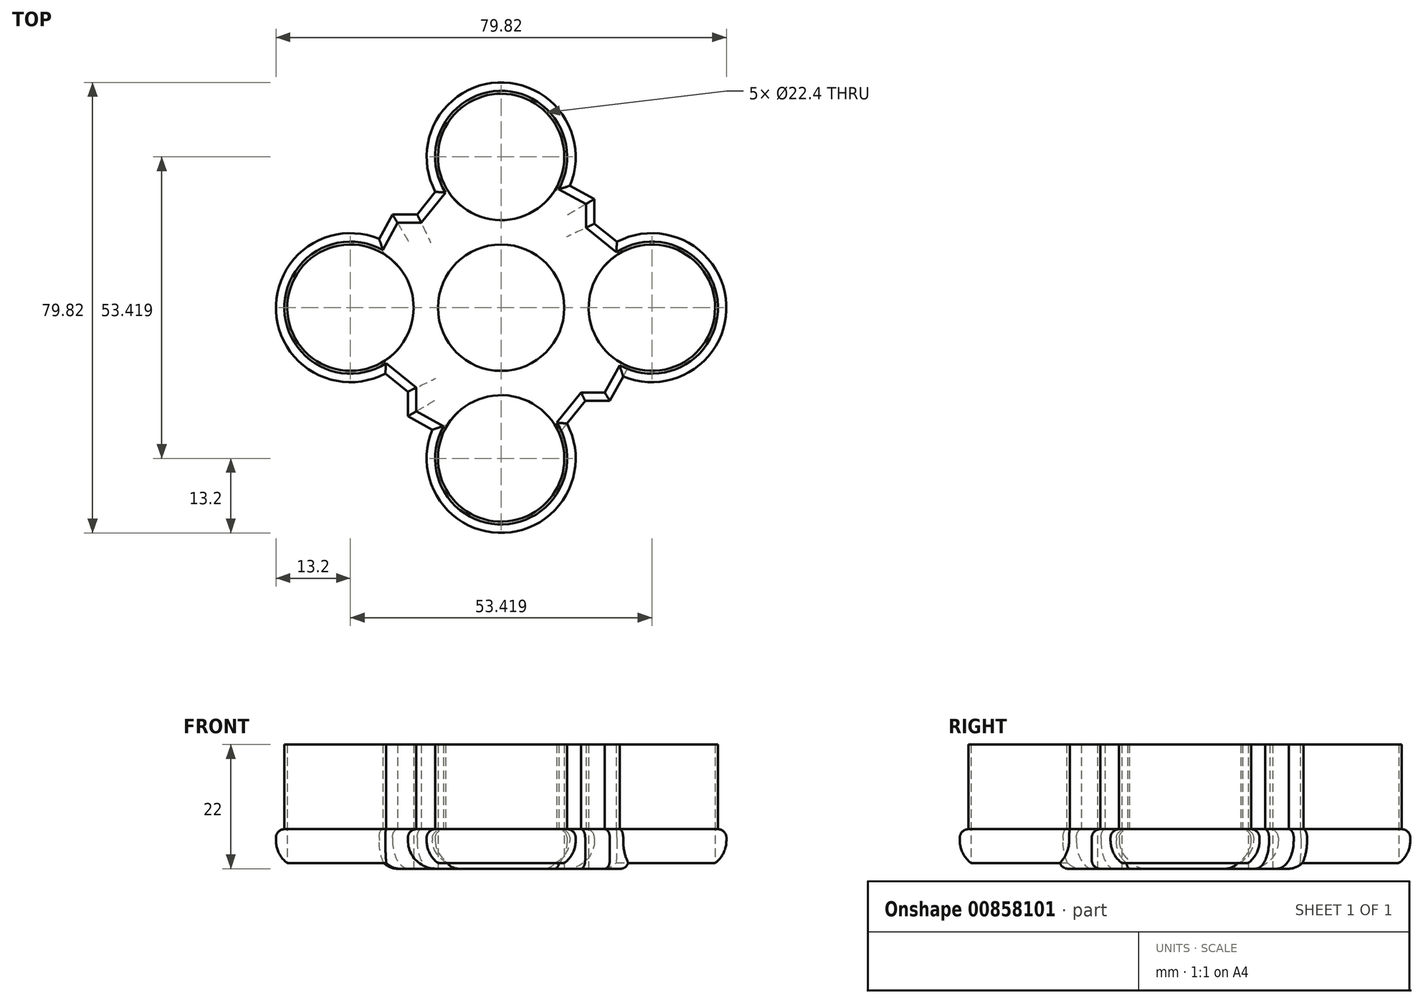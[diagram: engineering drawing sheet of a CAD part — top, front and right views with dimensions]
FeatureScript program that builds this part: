
annotation { "Feature Type Name" : "Feature", "Feature Type Description" : "" }
export const myFeature = defineFeature(function(context is Context, id is Id, definition is map)
    precondition{}
    {
        {
            var Q0;
            Q0=qCreatedBy(makeId("Top.planeOp"),FACE);
            var sketch = newSketch(context, id + "F0", { "sketchPlane" : qUnion([Q0])});
            skCircle(sketch, "E0", {"center": v(0, 0) * mm, "radius": 11.2 * mm});
            skCircle(sketch, "E1", {"center": v(0, 26.7) * mm, "radius": 11.2 * mm});
            skArc(sketch, "E2", {"start": v(12.18, 21.62) * mm, "mid": v(-0.6, 39.9) * mm, "end": v(-11.67, 20.53) * mm});
            skArc(sketch, "E3.1.0", {"start": v(-21.62, 12.18) * mm, "mid": v(-39.9, -0.6) * mm, "end": v(-20.53, -11.67) * mm});
            skCircle(sketch, "E3.1.1", {"center": v(-26.7, 0) * mm, "radius": 11.2 * mm});
            skArc(sketch, "E3.2.0", {"start": v(-12.18, -21.62) * mm, "mid": v(0.6, -39.9) * mm, "end": v(11.67, -20.53) * mm});
            skCircle(sketch, "E3.2.1", {"center": v(0, -26.7) * mm, "radius": 11.2 * mm});
            skArc(sketch, "E3.3.0", {"start": v(21.62, -12.18) * mm, "mid": v(39.9, 0.6) * mm, "end": v(20.53, 11.67) * mm});
            skCircle(sketch, "E3.3.1", {"center": v(26.7, 0) * mm, "radius": 11.2 * mm});
            skLineSegment(sketch, "E4", {"start": v(12.18, 21.62) * mm, "end": v(16.53, 19.26) * mm});
            skLineSegment(sketch, "E5", {"start": v(16.53, 19.26) * mm, "end": v(16.53, 14.9) * mm});
            skLineSegment(sketch, "E6", {"start": v(16.53, 14.9) * mm, "end": v(20.53, 11.67) * mm});
            skLineSegment(sketch, "E7.1.0", {"start": v(-21.62, 12.18) * mm, "end": v(-19.26, 16.53) * mm});
            skLineSegment(sketch, "E7.1.1", {"start": v(-19.26, 16.53) * mm, "end": v(-14.9, 16.53) * mm});
            skLineSegment(sketch, "E7.1.2", {"start": v(-14.9, 16.53) * mm, "end": v(-11.67, 20.53) * mm});
            skLineSegment(sketch, "E7.2.0", {"start": v(-12.18, -21.62) * mm, "end": v(-16.53, -19.26) * mm});
            skLineSegment(sketch, "E7.2.1", {"start": v(-16.53, -19.26) * mm, "end": v(-16.53, -14.9) * mm});
            skLineSegment(sketch, "E7.2.2", {"start": v(-16.53, -14.9) * mm, "end": v(-20.53, -11.67) * mm});
            skLineSegment(sketch, "E7.3.0", {"start": v(21.62, -12.18) * mm, "end": v(19.26, -16.53) * mm});
            skLineSegment(sketch, "E7.3.1", {"start": v(19.26, -16.53) * mm, "end": v(14.9, -16.53) * mm});
            skLineSegment(sketch, "E7.3.2", {"start": v(14.9, -16.53) * mm, "end": v(11.67, -20.53) * mm});
            skSolve(sketch);
        }
        {
            var Q0;
            Q0=makeQuery(id+"F0.imprint","IMPRINT",FACE,{"disambiguationData":[TD([[makeQuery(id+"F0.imprint","IMPRINT",EDGE,{"derivedFrom":sQuery(id+"F0.wireOp",EDGE,"E0")}),-1.0]])]});
            extrude(context, id + "F1", {"entities" : qUnion([Q0]), "depth" : 7 * mm, "offsetDistance" : 25 * mm});
        }
        {
            var Q0;
            Q0=makeQuery(id+"F1.opExtrude","CAP_EDGE",EDGE,{"disambiguationData":[OSD([sQuery(id+"F0.wireOp",EDGE,"E7.3.0")])],"isStart":false});
            var Q1;
            Q1=makeQuery(id+"F1.opExtrude","CAP_EDGE",EDGE,{"disambiguationData":[OSD([sQuery(id+"F0.wireOp",EDGE,"E7.3.2")])],"isStart":false});
            var Q2;
            Q2=makeQuery(id+"F1.opExtrude","CAP_EDGE",EDGE,{"disambiguationData":[OSD([sQuery(id+"F0.wireOp",EDGE,"E7.3.1")])],"isStart":false});
            var Q3;
            Q3=makeQuery(id+"F1.opExtrude","CAP_EDGE",EDGE,{"disambiguationData":[OSD([sQuery(id+"F0.wireOp",EDGE,"E3.2.0")])],"isStart":false});
            var Q4;
            Q4=makeQuery(id+"F1.opExtrude","CAP_EDGE",EDGE,{"disambiguationData":[OSD([sQuery(id+"F0.wireOp",EDGE,"E3.1.0")])],"isStart":false});
            var Q5;
            Q5=makeQuery(id+"F1.opExtrude","CAP_EDGE",EDGE,{"disambiguationData":[OSD([sQuery(id+"F0.wireOp",EDGE,"E2")])],"isStart":false});
            var Q6;
            Q6=makeQuery(id+"F1.opExtrude","CAP_EDGE",EDGE,{"disambiguationData":[OSD([sQuery(id+"F0.wireOp",EDGE,"E3.3.0")])],"isStart":false});
            var Q7;
            Q7=makeQuery(id+"F1.opExtrude","CAP_EDGE",EDGE,{"disambiguationData":[OSD([sQuery(id+"F0.wireOp",EDGE,"E7.1.0")])],"isStart":false});
            var Q8;
            Q8=makeQuery(id+"F1.opExtrude","CAP_EDGE",EDGE,{"disambiguationData":[OSD([sQuery(id+"F0.wireOp",EDGE,"E7.1.2")])],"isStart":false});
            var Q9;
            Q9=makeQuery(id+"F1.opExtrude","CAP_EDGE",EDGE,{"disambiguationData":[OSD([sQuery(id+"F0.wireOp",EDGE,"E7.1.1")])],"isStart":false});
            var Q10;
            Q10=makeQuery(id+"F1.opExtrude","CAP_EDGE",EDGE,{"disambiguationData":[OSD([sQuery(id+"F0.wireOp",EDGE,"E6")])],"isStart":false});
            var Q11;
            Q11=makeQuery(id+"F1.opExtrude","CAP_EDGE",EDGE,{"disambiguationData":[OSD([sQuery(id+"F0.wireOp",EDGE,"E5")])],"isStart":false});
            var Q12;
            Q12=makeQuery(id+"F1.opExtrude","CAP_EDGE",EDGE,{"disambiguationData":[OSD([sQuery(id+"F0.wireOp",EDGE,"E4")])],"isStart":false});
            var Q13;
            Q13=makeQuery(id+"F1.opExtrude","CAP_EDGE",EDGE,{"disambiguationData":[OSD([sQuery(id+"F0.wireOp",EDGE,"E7.2.0")])],"isStart":false});
            var Q14;
            Q14=makeQuery(id+"F1.opExtrude","CAP_EDGE",EDGE,{"disambiguationData":[OSD([sQuery(id+"F0.wireOp",EDGE,"E7.2.2")])],"isStart":false});
            var Q15;
            Q15=makeQuery(id+"F1.opExtrude","CAP_EDGE",EDGE,{"disambiguationData":[OSD([sQuery(id+"F0.wireOp",EDGE,"E7.2.1")])],"isStart":false});
            fillet(context, id + "F2", {"entities" : qUnion([Q0, Q1, Q2, Q3, Q4, Q5, Q6, Q7, Q8, Q9, Q10, Q11, Q12, Q13, Q14, Q15]), "radius" : 1.5 * mm, "tangentPropagation" : true, "allowEdgeOverflow" : false});
        }
        {
            var Q0;
            Q0=makeQuery(id+"F1.opExtrude","CAP_EDGE",EDGE,{"disambiguationData":[OSD([sQuery(id+"F0.wireOp",EDGE,"E7.3.2")])],"isStart":true});
            var Q1;
            Q1=makeQuery(id+"F1.opExtrude","CAP_EDGE",EDGE,{"disambiguationData":[OSD([sQuery(id+"F0.wireOp",EDGE,"E7.3.0")])],"isStart":true});
            var Q2;
            Q2=makeQuery(id+"F1.opExtrude","CAP_EDGE",EDGE,{"disambiguationData":[OSD([sQuery(id+"F0.wireOp",EDGE,"E7.3.1")])],"isStart":true});
            fillet(context, id + "F3", {"entities" : qUnion([Q0, Q1, Q2]), "radius" : 1.5 * mm, "tangentPropagation" : true, "allowEdgeOverflow" : false});
        }
        {
            var Q0;
            Q0=makeQuery(id+"F1.opExtrude","CAP_EDGE",EDGE,{"disambiguationData":[OSD([sQuery(id+"F0.wireOp",EDGE,"E3.2.0")])],"isStart":true});
            var Q1;
            Q1=makeQuery(id+"F1.opExtrude","CAP_EDGE",EDGE,{"disambiguationData":[OSD([sQuery(id+"F0.wireOp",EDGE,"E7.2.0")])],"isStart":true});
            var Q2;
            Q2=makeQuery(id+"F1.opExtrude","CAP_EDGE",EDGE,{"disambiguationData":[OSD([sQuery(id+"F0.wireOp",EDGE,"E3.1.0")])],"isStart":true});
            var Q3;
            Q3=makeQuery(id+"F1.opExtrude","CAP_EDGE",EDGE,{"disambiguationData":[OSD([sQuery(id+"F0.wireOp",EDGE,"E2")])],"isStart":true});
            var Q4;
            Q4=makeQuery(id+"F1.opExtrude","CAP_EDGE",EDGE,{"disambiguationData":[OSD([sQuery(id+"F0.wireOp",EDGE,"E3.3.0")])],"isStart":true});
            var Q5;
            Q5=makeQuery(id+"F1.opExtrude","CAP_EDGE",EDGE,{"disambiguationData":[OSD([sQuery(id+"F0.wireOp",EDGE,"E6")])],"isStart":true});
            var Q6;
            Q6=makeQuery(id+"F1.opExtrude","CAP_EDGE",EDGE,{"disambiguationData":[OSD([sQuery(id+"F0.wireOp",EDGE,"E5")])],"isStart":true});
            var Q7;
            Q7=makeQuery(id+"F1.opExtrude","CAP_EDGE",EDGE,{"disambiguationData":[OSD([sQuery(id+"F0.wireOp",EDGE,"E7.1.2")])],"isStart":true});
            var Q8;
            Q8=makeQuery(id+"F1.opExtrude","CAP_EDGE",EDGE,{"disambiguationData":[OSD([sQuery(id+"F0.wireOp",EDGE,"E7.1.0")])],"isStart":true});
            var Q9;
            Q9=makeQuery(id+"F1.opExtrude","CAP_EDGE",EDGE,{"disambiguationData":[OSD([sQuery(id+"F0.wireOp",EDGE,"E7.2.2")])],"isStart":true});
            var Q10;
            Q10=makeQuery(id+"F1.opExtrude","CAP_EDGE",EDGE,{"disambiguationData":[OSD([sQuery(id+"F0.wireOp",EDGE,"E7.1.1")])],"isStart":true});
            var Q11;
            Q11=makeQuery(id+"F1.opExtrude","CAP_EDGE",EDGE,{"disambiguationData":[OSD([sQuery(id+"F0.wireOp",EDGE,"E7.2.1")])],"isStart":true});
            var Q12;
            Q12=makeQuery(id+"F1.opExtrude","CAP_EDGE",EDGE,{"disambiguationData":[OSD([sQuery(id+"F0.wireOp",EDGE,"E4")])],"isStart":true});
            fillet(context, id + "F4", {"entities" : qUnion([Q0, Q1, Q2, Q3, Q4, Q5, Q6, Q7, Q8, Q9, Q10, Q11, Q12]), "radius" : 5 * mm, "tangentPropagation" : true, "allowEdgeOverflow" : false});
        }
        {
            var Q0;
            Q0=makeQuery(id+"F1.opExtrude","CAP_FACE",FACE,{"disambiguationData":[OSD([sQuery(id+"F0.wireOp",EDGE,"E0"),sQuery(id+"F0.wireOp",EDGE,"E1"),sQuery(id+"F0.wireOp",EDGE,"E2"),sQuery(id+"F0.wireOp",EDGE,"E3.1.0"),sQuery(id+"F0.wireOp",EDGE,"E3.1.1"),sQuery(id+"F0.wireOp",EDGE,"E3.2.0"),sQuery(id+"F0.wireOp",EDGE,"E3.2.1"),sQuery(id+"F0.wireOp",EDGE,"E3.3.0"),sQuery(id+"F0.wireOp",EDGE,"E3.3.1"),sQuery(id+"F0.wireOp",EDGE,"E4"),sQuery(id+"F0.wireOp",EDGE,"E5"),sQuery(id+"F0.wireOp",EDGE,"E6"),sQuery(id+"F0.wireOp",EDGE,"E7.1.0"),sQuery(id+"F0.wireOp",EDGE,"E7.1.1"),sQuery(id+"F0.wireOp",EDGE,"E7.1.2"),sQuery(id+"F0.wireOp",EDGE,"E7.2.0"),sQuery(id+"F0.wireOp",EDGE,"E7.2.1"),sQuery(id+"F0.wireOp",EDGE,"E7.2.2"),sQuery(id+"F0.wireOp",EDGE,"E7.3.0"),sQuery(id+"F0.wireOp",EDGE,"E7.3.1"),sQuery(id+"F0.wireOp",EDGE,"E7.3.2")])],"isStart":false});
            extrude(context, id + "F5", {"entities" : qUnion([Q0]), "operationType" : NewBodyOperationType.ADD, "depth" : 5 * mm, "offsetDistance" : 25 * mm});
        }
        {
            var Q0;
            Q0=makeQuery(id+"F5.opExtrude","CAP_FACE",FACE,{"disambiguationData":[OSD([sQuery(id+"F0.wireOp",EDGE,"E0"),sQuery(id+"F0.wireOp",EDGE,"E1"),sQuery(id+"F0.wireOp",EDGE,"E2"),sQuery(id+"F0.wireOp",EDGE,"E3.1.0"),sQuery(id+"F0.wireOp",EDGE,"E3.1.1"),sQuery(id+"F0.wireOp",EDGE,"E3.2.0"),sQuery(id+"F0.wireOp",EDGE,"E3.2.1"),sQuery(id+"F0.wireOp",EDGE,"E3.3.0"),sQuery(id+"F0.wireOp",EDGE,"E3.3.1"),sQuery(id+"F0.wireOp",EDGE,"E4"),sQuery(id+"F0.wireOp",EDGE,"E5"),sQuery(id+"F0.wireOp",EDGE,"E6"),sQuery(id+"F0.wireOp",EDGE,"E7.1.0"),sQuery(id+"F0.wireOp",EDGE,"E7.1.1"),sQuery(id+"F0.wireOp",EDGE,"E7.1.2"),sQuery(id+"F0.wireOp",EDGE,"E7.2.0"),sQuery(id+"F0.wireOp",EDGE,"E7.2.1"),sQuery(id+"F0.wireOp",EDGE,"E7.2.2"),sQuery(id+"F0.wireOp",EDGE,"E7.3.0"),sQuery(id+"F0.wireOp",EDGE,"E7.3.1"),sQuery(id+"F0.wireOp",EDGE,"E7.3.2")])],"isStart":false});
            extrude(context, id + "F6", {"entities" : qUnion([Q0]), "operationType" : NewBodyOperationType.ADD, "depth" : 5 * mm, "offsetDistance" : 25 * mm});
        }
        {
            var Q0;
            Q0=makeQuery(id+"F6.opExtrude","CAP_FACE",FACE,{"disambiguationData":[OSD([sQuery(id+"F0.wireOp",EDGE,"E0"),sQuery(id+"F0.wireOp",EDGE,"E1"),sQuery(id+"F0.wireOp",EDGE,"E2"),sQuery(id+"F0.wireOp",EDGE,"E3.1.0"),sQuery(id+"F0.wireOp",EDGE,"E3.1.1"),sQuery(id+"F0.wireOp",EDGE,"E3.2.0"),sQuery(id+"F0.wireOp",EDGE,"E3.2.1"),sQuery(id+"F0.wireOp",EDGE,"E3.3.0"),sQuery(id+"F0.wireOp",EDGE,"E3.3.1"),sQuery(id+"F0.wireOp",EDGE,"E4"),sQuery(id+"F0.wireOp",EDGE,"E5"),sQuery(id+"F0.wireOp",EDGE,"E6"),sQuery(id+"F0.wireOp",EDGE,"E7.1.0"),sQuery(id+"F0.wireOp",EDGE,"E7.1.1"),sQuery(id+"F0.wireOp",EDGE,"E7.1.2"),sQuery(id+"F0.wireOp",EDGE,"E7.2.0"),sQuery(id+"F0.wireOp",EDGE,"E7.2.1"),sQuery(id+"F0.wireOp",EDGE,"E7.2.2"),sQuery(id+"F0.wireOp",EDGE,"E7.3.0"),sQuery(id+"F0.wireOp",EDGE,"E7.3.1"),sQuery(id+"F0.wireOp",EDGE,"E7.3.2")])],"isStart":false});
            extrude(context, id + "F7", {"entities" : qUnion([Q0]), "operationType" : NewBodyOperationType.ADD, "depth" : 5 * mm, "offsetDistance" : 25 * mm});
        }
    });
